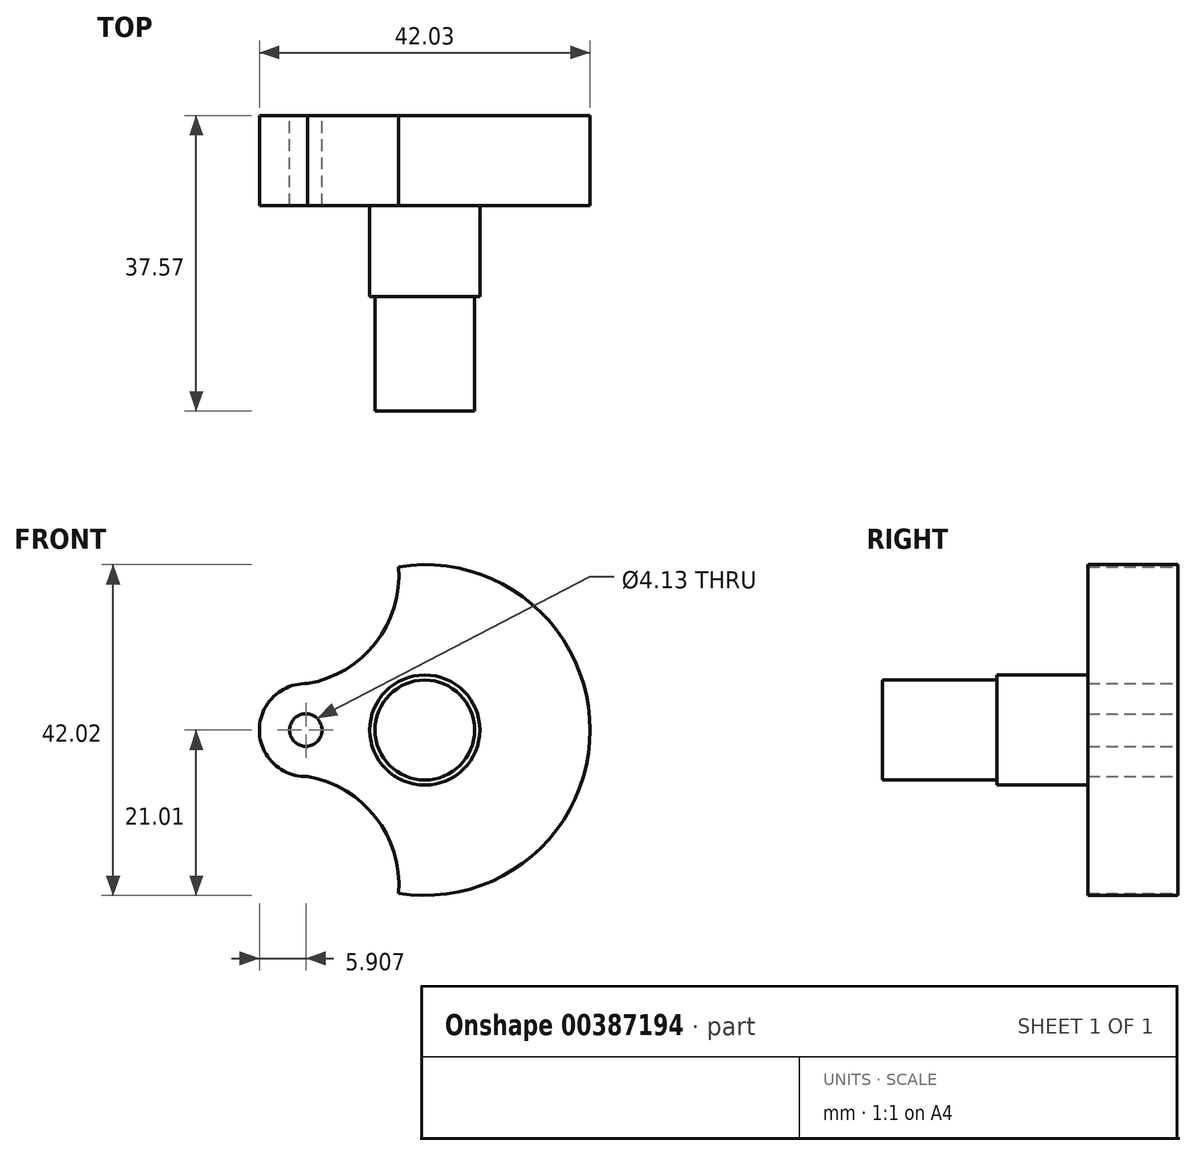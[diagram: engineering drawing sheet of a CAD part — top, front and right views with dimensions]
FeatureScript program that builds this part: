
annotation { "Feature Type Name" : "Feature", "Feature Type Description" : "" }
export const myFeature = defineFeature(function(context is Context, id is Id, definition is map)
    precondition{}
    {
        {
            var Q0;
            Q0=qCreatedBy(makeId("Front.planeOp"),FACE);
            var sketch = newSketch(context, id + "F0", { "sketchPlane" : qUnion([Q0])});
            skArc(sketch, "E0", {"start": v(-3.32, -20.74) * mm, "mid": v(21, 0) * mm, "end": v(-3.32, 20.74) * mm});
            skPoint(sketch, "E1", {"position": v(-15.11, 0) * mm});
            skArc(sketch, "E2", {"start": v(-14.89, 5.9) * mm, "mid": v(-21.02, 0) * mm, "end": v(-14.89, -5.9) * mm});
            skArc(sketch, "E3", {"start": v(-3.32, -20.74) * mm, "mid": v(-6.8, -10.42) * mm, "end": v(-16.61, -5.71) * mm});
            skPoint(sketch, "E3.first.point", {"position": v(-14.89, -5.9) * mm});
            skPoint(sketch, "E3.second.point", {"position": v(-12.16, -32.72) * mm});
            skPoint(sketch, "E3.third.point", {"position": v(-16.61, -5.71) * mm});
            skArc(sketch, "E4.MirrorCS", {"start": v(-3.32, 20.74) * mm, "mid": v(-6.8, 10.42) * mm, "end": v(-16.61, 5.71) * mm});
            skArc(sketch, "E5.trimOffspring", {"start": v(-21, 0.46) * mm, "mid": v(-21, 0) * mm, "end": v(-21, -0.46) * mm});
            skCircle(sketch, "E6", {"center": v(-15.11, 0) * mm, "radius": 2.07 * mm});
            skCircle(sketch, "E7", {"center": v(0, 0) * mm, "radius": 7 * mm});
            skCircle(sketch, "E8", {"center": v(0, 0) * mm, "radius": 6.34 * mm});
            skSolve(sketch);
        }
        {
            var Q0;
            Q0 = qSketchRegion(id + "F0", true);
            extrude(context, id + "F1", {"entities" : qUnion([Q0]), "depth" : 11.43 * mm});
        }
        {
            var Q0;
            Q0=makeQuery(id+"F0.imprint","IMPRINT",FACE,{"disambiguationData":[TD([[makeQuery(id+"F0.imprint","IMPRINT",EDGE,{"derivedFrom":sQuery(id+"F0.wireOp",EDGE,"E7")}),1.0]])]});
            extrude(context, id + "F2", {"entities" : qUnion([Q0]), "operationType" : NewBodyOperationType.ADD, "depth" : 23.01 * mm});
        }
        {
            var Q0;
            Q0=makeQuery(id+"F0.imprint","IMPRINT",FACE,{"disambiguationData":[TD([[makeQuery(id+"F0.imprint","IMPRINT",EDGE,{"derivedFrom":sQuery(id+"F0.wireOp",EDGE,"E8")}),1.0]])]});
            extrude(context, id + "F3", {"entities" : qUnion([Q0]), "operationType" : NewBodyOperationType.ADD, "depth" : 37.57 * mm});
        }
    });
